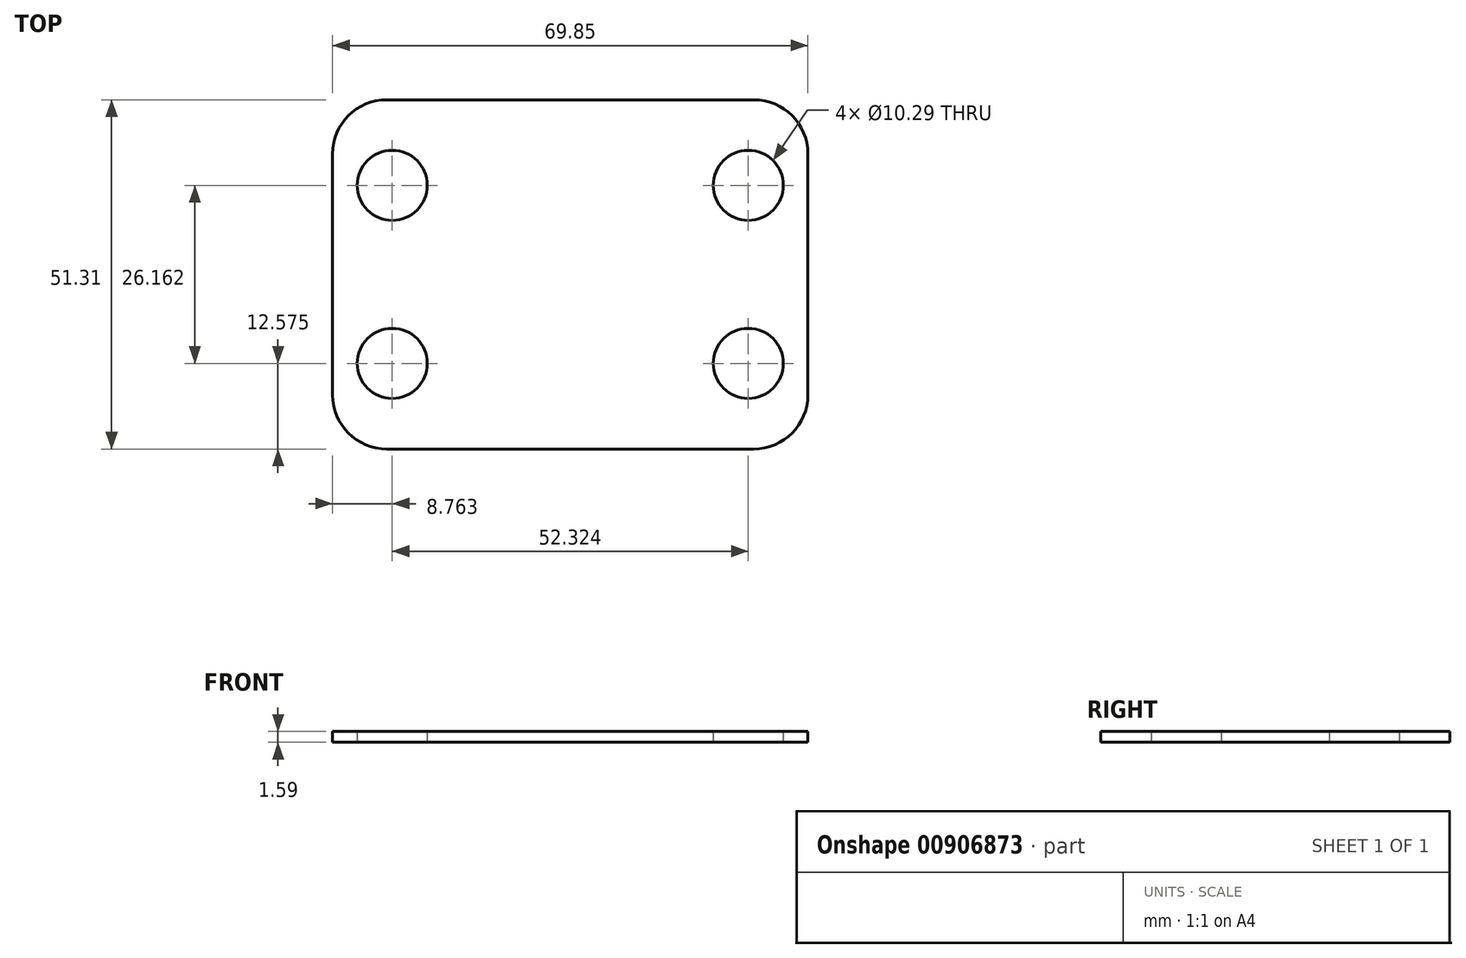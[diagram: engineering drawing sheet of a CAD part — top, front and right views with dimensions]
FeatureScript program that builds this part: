
annotation { "Feature Type Name" : "Feature", "Feature Type Description" : "" }
export const myFeature = defineFeature(function(context is Context, id is Id, definition is map)
    precondition{}
    {
        {
            var Q0;
            Q0=qCreatedBy(makeId("Top.planeOp"),FACE);
            var sketch = newSketch(context, id + "F0", { "sketchPlane" : qUnion([Q0])});
            skLineSegment(sketch, "E0.bottom", {"start": v(7.94, 0) * mm, "end": v(61.91, 0) * mm});
            skLineSegment(sketch, "E0.top", {"start": v(7.94, -51.3) * mm, "end": v(61.91, -51.3) * mm});
            skLineSegment(sketch, "E0.left", {"start": v(0, -7.94) * mm, "end": v(0, -43.37) * mm});
            skLineSegment(sketch, "E0.right", {"start": v(69.85, -7.94) * mm, "end": v(69.85, -43.37) * mm});
            skCircle(sketch, "E1", {"center": v(8.76, -12.57) * mm, "radius": 5.14 * mm});
            skCircle(sketch, "E2", {"center": v(61.09, -12.57) * mm, "radius": 5.14 * mm});
            skCircle(sketch, "E3", {"center": v(8.76, -38.74) * mm, "radius": 5.14 * mm});
            skCircle(sketch, "E4", {"center": v(61.09, -38.74) * mm, "radius": 5.14 * mm});
            skLineSegment(sketch, "E5", {"start": v(34.93, 0) * mm, "end": v(34.93, -51.3) * mm, "construction": true});
            skLineSegment(sketch, "E6", {"start": v(0, -25.65) * mm, "end": v(69.85, -25.65) * mm, "construction": true});
            skPoint(sketch, "E7.visualSharp", {"position": v(0, 0) * mm});
            skArc(sketch, "E7.filletArc", {"start": v(7.94, 0) * mm, "mid": v(2.32, -2.32) * mm, "end": v(0, -7.94) * mm});
            skPoint(sketch, "E8.visualSharp", {"position": v(69.85, 0) * mm});
            skArc(sketch, "E8.filletArc", {"start": v(69.85, -7.94) * mm, "mid": v(67.53, -2.32) * mm, "end": v(61.91, 0) * mm});
            skPoint(sketch, "E9.visualSharp", {"position": v(69.85, -51.3) * mm});
            skArc(sketch, "E9.filletArc", {"start": v(61.91, -51.3) * mm, "mid": v(67.53, -48.98) * mm, "end": v(69.85, -43.37) * mm});
            skPoint(sketch, "E10.visualSharp", {"position": v(0, -51.3) * mm});
            skArc(sketch, "E10.filletArc", {"start": v(0, -43.37) * mm, "mid": v(2.32, -48.98) * mm, "end": v(7.94, -51.3) * mm});
            skSolve(sketch);
        }
        {
            var Q0;
            Q0 = qSketchRegion(id + "F0", true);
            extrude(context, id + "F1", {"entities" : qUnion([Q0]), "depth" : 1.59 * mm, "offsetDistance" : 25.4 * mm});
        }
    });
